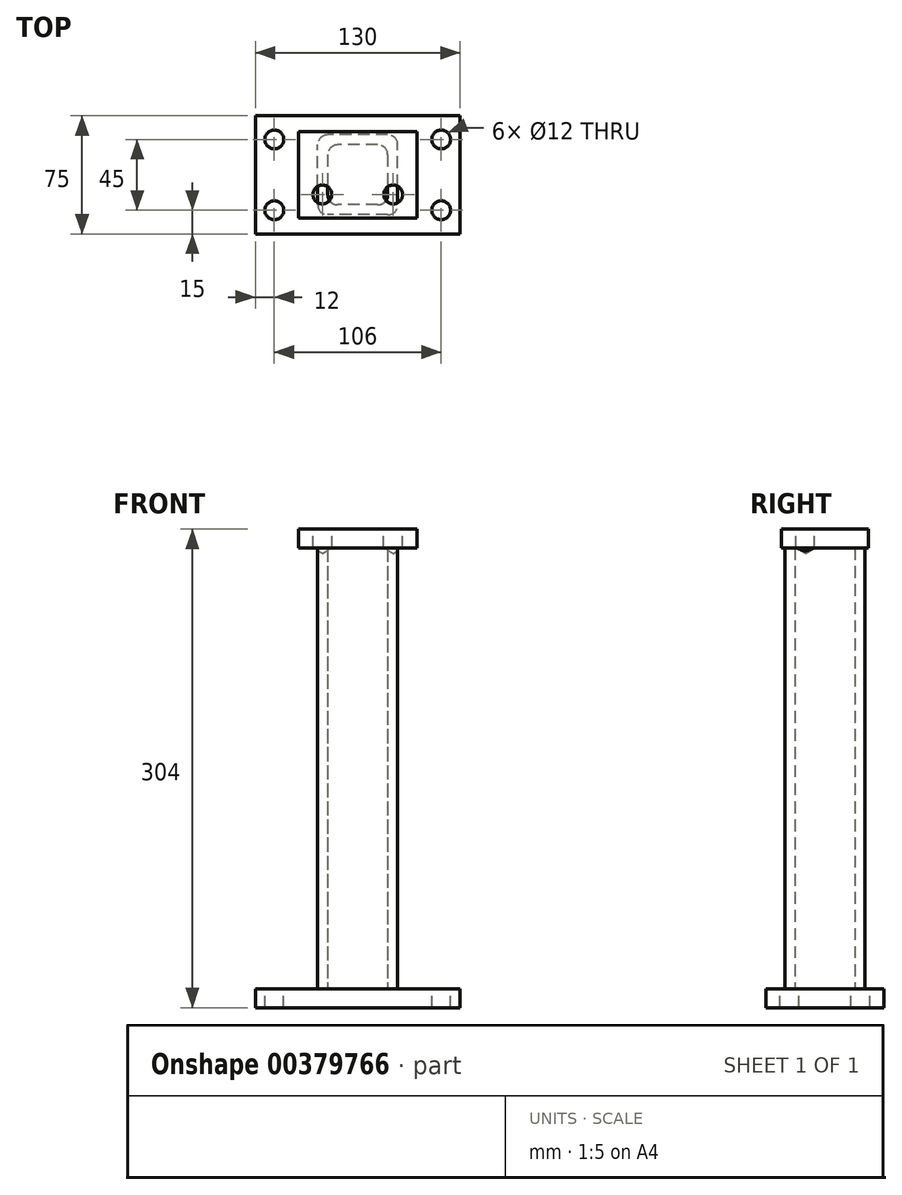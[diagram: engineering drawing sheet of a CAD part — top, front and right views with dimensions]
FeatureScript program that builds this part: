
annotation { "Feature Type Name" : "Feature", "Feature Type Description" : "" }
export const myFeature = defineFeature(function(context is Context, id is Id, definition is map)
    precondition{}
    {
        {
            var Q0;
            Q0=qCreatedBy(makeId("Top.planeOp"),FACE);
            var sketch = newSketch(context, id + "F0", { "sketchPlane" : qUnion([Q0])});
            skLineSegment(sketch, "E0.bottom", {"start": v(65, 37.5) * mm, "end": v(-65, 37.5) * mm});
            skLineSegment(sketch, "E0.top", {"start": v(65, -37.5) * mm, "end": v(-65, -37.5) * mm});
            skLineSegment(sketch, "E0.left", {"start": v(65, 37.5) * mm, "end": v(65, -37.5) * mm});
            skLineSegment(sketch, "E0.right", {"start": v(-65, 37.5) * mm, "end": v(-65, -37.5) * mm});
            skPoint(sketch, "E0.middle", {"position": v(0, 0) * mm});
            skSolve(sketch);
        }
        {
            var Q0;
            Q0=makeQuery(id+"F0.imprint","IMPRINT",FACE,{"disambiguationData":[TD([[makeQuery(id+"F0.imprint","IMPRINT",EDGE,{"derivedFrom":sQuery(id+"F0.wireOp",EDGE,"E0.bottom")}),1.0]])]});
            extrude(context, id + "F1", {"entities" : qUnion([Q0]), "depth" : -12 * mm});
        }
        {
            var Q0;
            Q0=makeQuery(id+"F1.opExtrude","CAP_FACE",FACE,{"disambiguationData":[OSD([sQuery(id+"F0.wireOp",EDGE,"E0.bottom"),sQuery(id+"F0.wireOp",EDGE,"E0.top"),sQuery(id+"F0.wireOp",EDGE,"E0.left"),sQuery(id+"F0.wireOp",EDGE,"E0.right")])],"isStart":true});
            var sketch = newSketch(context, id + "F2", { "sketchPlane" : qUnion([Q0])});
            skLineSegment(sketch, "E1.bottom", {"start": v(19.05, -25.4) * mm, "end": v(-19.05, -25.4) * mm});
            skLineSegment(sketch, "E1.top", {"start": v(19.05, 25.4) * mm, "end": v(-19.05, 25.4) * mm});
            skLineSegment(sketch, "E1.left", {"start": v(25.4, -19.05) * mm, "end": v(25.4, 19.05) * mm});
            skLineSegment(sketch, "E1.right", {"start": v(-25.4, -19.05) * mm, "end": v(-25.4, 19.05) * mm});
            skPoint(sketch, "E1.middle", {"position": v(0, 0) * mm});
            skPoint(sketch, "E2.visualSharp", {"position": v(-25.4, -25.4) * mm});
            skArc(sketch, "E2.filletArc", {"start": v(-25.4, -19.05) * mm, "mid": v(-23.54, -23.54) * mm, "end": v(-19.05, -25.4) * mm});
            skPoint(sketch, "E3.visualSharp", {"position": v(-25.4, 25.4) * mm});
            skArc(sketch, "E3.filletArc", {"start": v(-19.05, 25.4) * mm, "mid": v(-23.54, 23.54) * mm, "end": v(-25.4, 19.05) * mm});
            skPoint(sketch, "E4.visualSharp", {"position": v(25.4, 25.4) * mm});
            skArc(sketch, "E4.filletArc", {"start": v(25.4, 19.05) * mm, "mid": v(23.54, 23.54) * mm, "end": v(19.05, 25.4) * mm});
            skPoint(sketch, "E5.visualSharp", {"position": v(25.4, -25.4) * mm});
            skArc(sketch, "E5.filletArc", {"start": v(19.05, -25.4) * mm, "mid": v(23.54, -23.54) * mm, "end": v(25.4, -19.05) * mm});
            skLineSegment(sketch, "E6.bottom", {"start": v(12.7, 19.05) * mm, "end": v(-12.7, 19.05) * mm});
            skLineSegment(sketch, "E6.top", {"start": v(12.7, -19.05) * mm, "end": v(-12.7, -19.05) * mm});
            skLineSegment(sketch, "E6.left", {"start": v(19.05, 12.7) * mm, "end": v(19.05, -12.7) * mm});
            skLineSegment(sketch, "E6.right", {"start": v(-19.05, 12.7) * mm, "end": v(-19.05, -12.7) * mm});
            skArc(sketch, "E7.filletArc", {"start": v(-12.7, 19.05) * mm, "mid": v(-17.2, 17.2) * mm, "end": v(-19.05, 12.7) * mm});
            skArc(sketch, "E8.filletArc", {"start": v(19.05, 12.7) * mm, "mid": v(17.2, 17.2) * mm, "end": v(12.7, 19.05) * mm});
            skArc(sketch, "E9.filletArc", {"start": v(12.7, -19.05) * mm, "mid": v(17.2, -17.2) * mm, "end": v(19.05, -12.7) * mm});
            skArc(sketch, "E10.filletArc", {"start": v(-19.05, -12.7) * mm, "mid": v(-17.2, -17.2) * mm, "end": v(-12.7, -19.05) * mm});
            skSolve(sketch);
        }
        {
            var Q0;
            Q0=qSketchRegion(id+"F2",true);
            extrude(context, id + "F3", {"entities" : qUnion([Q0]), "operationType" : NewBodyOperationType.ADD, "depth" : (280) * mm});
        }
        {
            var Q0;
            {var subQ0=sQuery(id+"F0.wireOp",EDGE,"E0.left");var subQ1=sQuery(id+"F0.wireOp",EDGE,"E0.bottom");var subQ2=sQuery(id+"F0.wireOp",EDGE,"E0.right");var subQ3=sQuery(id+"F0.wireOp",EDGE,"E0.top");Q0=makeQuery(id+"F3.boolean.opBoolean","SPLIT",FACE,{"disambiguationData":[TD([makeQuery(id+"F1.opExtrude","SWEPT_FACE",FACE,{"disambiguationData":[OSD([subQ1])]})])],"derivedFrom":makeQuery(id+"F1.opExtrude","CAP_FACE",FACE,{"disambiguationData":[OSD([subQ1,subQ3,subQ0,subQ2])],"isStart":true})});}
            var sketch = newSketch(context, id + "F4", { "sketchPlane" : qUnion([Q0])});
            skLineSegment(sketch, "E11", {"start": v(-65, -37.5) * mm, "end": v(-53, -37.5) * mm, "construction": true});
            skLineSegment(sketch, "E12", {"start": v(-53, -37.5) * mm, "end": v(-53, -22.5) * mm, "construction": true});
            skLineSegment(sketch, "E13", {"start": v(-65, 37.5) * mm, "end": v(-53, 37.5) * mm, "construction": true});
            skLineSegment(sketch, "E14", {"start": v(-53, 37.5) * mm, "end": v(-53, 22.5) * mm, "construction": true});
            skLineSegment(sketch, "E15", {"start": v(65, 37.5) * mm, "end": v(53, 37.5) * mm, "construction": true});
            skLineSegment(sketch, "E16", {"start": v(65, -37.5) * mm, "end": v(53, -37.5) * mm, "construction": true});
            skLineSegment(sketch, "E17", {"start": v(53, -37.5) * mm, "end": v(53, -22.5) * mm, "construction": true});
            skLineSegment(sketch, "E18", {"start": v(53, 37.5) * mm, "end": v(53, 22.5) * mm, "construction": true});
            skSolve(sketch);
        }
        {
            var Q0;
            Q0=makeQuery(id+"F3.opExtrude","CAP_FACE",FACE,{"disambiguationData":[OSD([sQuery(id+"F2.wireOp",EDGE,"E1.bottom"),sQuery(id+"F2.wireOp",EDGE,"E1.top"),sQuery(id+"F2.wireOp",EDGE,"E1.left"),sQuery(id+"F2.wireOp",EDGE,"E1.right"),sQuery(id+"F2.wireOp",EDGE,"E2.filletArc"),sQuery(id+"F2.wireOp",EDGE,"E3.filletArc"),sQuery(id+"F2.wireOp",EDGE,"E4.filletArc"),sQuery(id+"F2.wireOp",EDGE,"E5.filletArc"),sQuery(id+"F2.wireOp",EDGE,"E6.bottom"),sQuery(id+"F2.wireOp",EDGE,"E6.top"),sQuery(id+"F2.wireOp",EDGE,"E6.left"),sQuery(id+"F2.wireOp",EDGE,"E6.right"),sQuery(id+"F2.wireOp",EDGE,"E7.filletArc"),sQuery(id+"F2.wireOp",EDGE,"E8.filletArc"),sQuery(id+"F2.wireOp",EDGE,"E9.filletArc"),sQuery(id+"F2.wireOp",EDGE,"E10.filletArc")])],"isStart":false});
            var sketch = newSketch(context, id + "F5", { "sketchPlane" : qUnion([Q0])});
            skLineSegment(sketch, "E19.bottom", {"start": v(37.5, -27.5) * mm, "end": v(-37.5, -27.5) * mm});
            skLineSegment(sketch, "E19.top", {"start": v(37.5, 27.5) * mm, "end": v(-37.5, 27.5) * mm});
            skLineSegment(sketch, "E19.left", {"start": v(37.5, -27.5) * mm, "end": v(37.5, 27.5) * mm});
            skLineSegment(sketch, "E19.right", {"start": v(-37.5, -27.5) * mm, "end": v(-37.5, 27.5) * mm});
            skPoint(sketch, "E19.middle", {"position": v(0, 0) * mm});
            skSolve(sketch);
        }
        {
            var Q0;
            Q0=makeQuery(id+"F5.imprint","IMPRINT",FACE,{"disambiguationData":[TD([[makeQuery(id+"F5.imprint","IMPRINT",EDGE,{"derivedFrom":makeQuery(id+"F3.opExtrude","CAP_EDGE",EDGE,{"disambiguationData":[OSD([sQuery(id+"F2.wireOp",EDGE,"E6.bottom")])],"isStart":false})}),1.0]])]});
            var Q1;
            Q1=makeQuery(id+"F5.imprint","IMPRINT",FACE,{"disambiguationData":[TD([[makeQuery(id+"F5.imprint","IMPRINT",EDGE,{"derivedFrom":sQuery(id+"F5.wireOp",EDGE,"E19.bottom")}),-1.0]])]});
            var Q2;
            Q2=makeQuery(id+"F5.imprint","IMPRINT",FACE,{"disambiguationData":[TD([[makeQuery(id+"F5.imprint","IMPRINT",EDGE,{"derivedFrom":makeQuery(id+"F3.opExtrude","CAP_EDGE",EDGE,{"disambiguationData":[OSD([sQuery(id+"F2.wireOp",EDGE,"E1.bottom")])],"isStart":false})}),-1.0]])]});
            extrude(context, id + "F6", {"entities" : qUnion([Q0, Q1, Q2]), "operationType" : NewBodyOperationType.ADD, "depth" : 12 * mm});
        }
        {
            var Q0;
            Q0=sQuery(id+"F4.wireOp",VERTEX,"E14.end");
            var Q1;
            Q1=sQuery(id+"F4.wireOp",VERTEX,"E18.end");
            var Q2;
            Q2=sQuery(id+"F4.wireOp",VERTEX,"E17.end");
            var Q3;
            Q3=sQuery(id+"F4.wireOp",VERTEX,"E12.end");
            var Q4;
            Q4=makeQuery(id+"F1.opExtrude","SWEPT_BODY",BODY,{"disambiguationData":[OSD([sQuery(id+"F0.wireOp",EDGE,"E0.bottom"),sQuery(id+"F0.wireOp",EDGE,"E0.top"),sQuery(id+"F0.wireOp",EDGE,"E0.left"),sQuery(id+"F0.wireOp",EDGE,"E0.right")])]});
            hole(context, id + "F7", {"style" : HoleStyle.SIMPLE, "endStyle" : HoleEndStyle.THROUGH, "holeDiameter" : 12 * mm, "isTappedThrough" : true, "tappedDepth" : 12 * mm, "tapClearance" : 3, "locations" : qUnion([Q0, Q1, Q2, Q3]), "scope" : qUnion([Q4])});
        }
        {
            var Q0;
            Q0=makeQuery(id+"F6.opExtrude","CAP_FACE",FACE,{"disambiguationData":[OSD([sQuery(id+"F5.wireOp",EDGE,"E19.bottom"),sQuery(id+"F5.wireOp",EDGE,"E19.top"),sQuery(id+"F5.wireOp",EDGE,"E19.left"),sQuery(id+"F5.wireOp",EDGE,"E19.right")])],"isStart":false});
            var sketch = newSketch(context, id + "F8", { "sketchPlane" : qUnion([Q0])});
            skLineSegment(sketch, "E20", {"start": v(37.5, -27.5) * mm, "end": v(37.5, -12.5) * mm, "construction": true});
            skLineSegment(sketch, "E21", {"start": v(37.5, -12.5) * mm, "end": v(22.5, -12.5) * mm, "construction": true});
            skLineSegment(sketch, "E22", {"start": v(22.5, -12.5) * mm, "end": v(-22.5, -12.5) * mm, "construction": true});
            skLineSegment(sketch, "E23", {"start": v(-22.5, -12.5) * mm, "end": v(-37.5, -12.5) * mm, "construction": true});
            skSolve(sketch);
        }
        {
            var Q0;
            Q0=sQuery(id+"F8.wireOp",VERTEX,"E23.start");
            var Q1;
            Q1=sQuery(id+"F8.wireOp",VERTEX,"E22.start");
            var Q2;
            Q2=makeQuery(id+"F1.opExtrude","SWEPT_BODY",BODY,{"disambiguationData":[OSD([sQuery(id+"F0.wireOp",EDGE,"E0.bottom"),sQuery(id+"F0.wireOp",EDGE,"E0.top"),sQuery(id+"F0.wireOp",EDGE,"E0.left"),sQuery(id+"F0.wireOp",EDGE,"E0.right")])]});
            hole(context, id + "F9", {"style" : HoleStyle.SIMPLE, "endStyle" : HoleEndStyle.BLIND, "holeDiameter" : 12 * mm, "holeDepth" : 12 * mm, "isTappedThrough" : true, "tappedDepth" : 12 * mm, "tapClearance" : 3, "locations" : qUnion([Q0, Q1]), "scope" : qUnion([Q2])});
        }
    });
